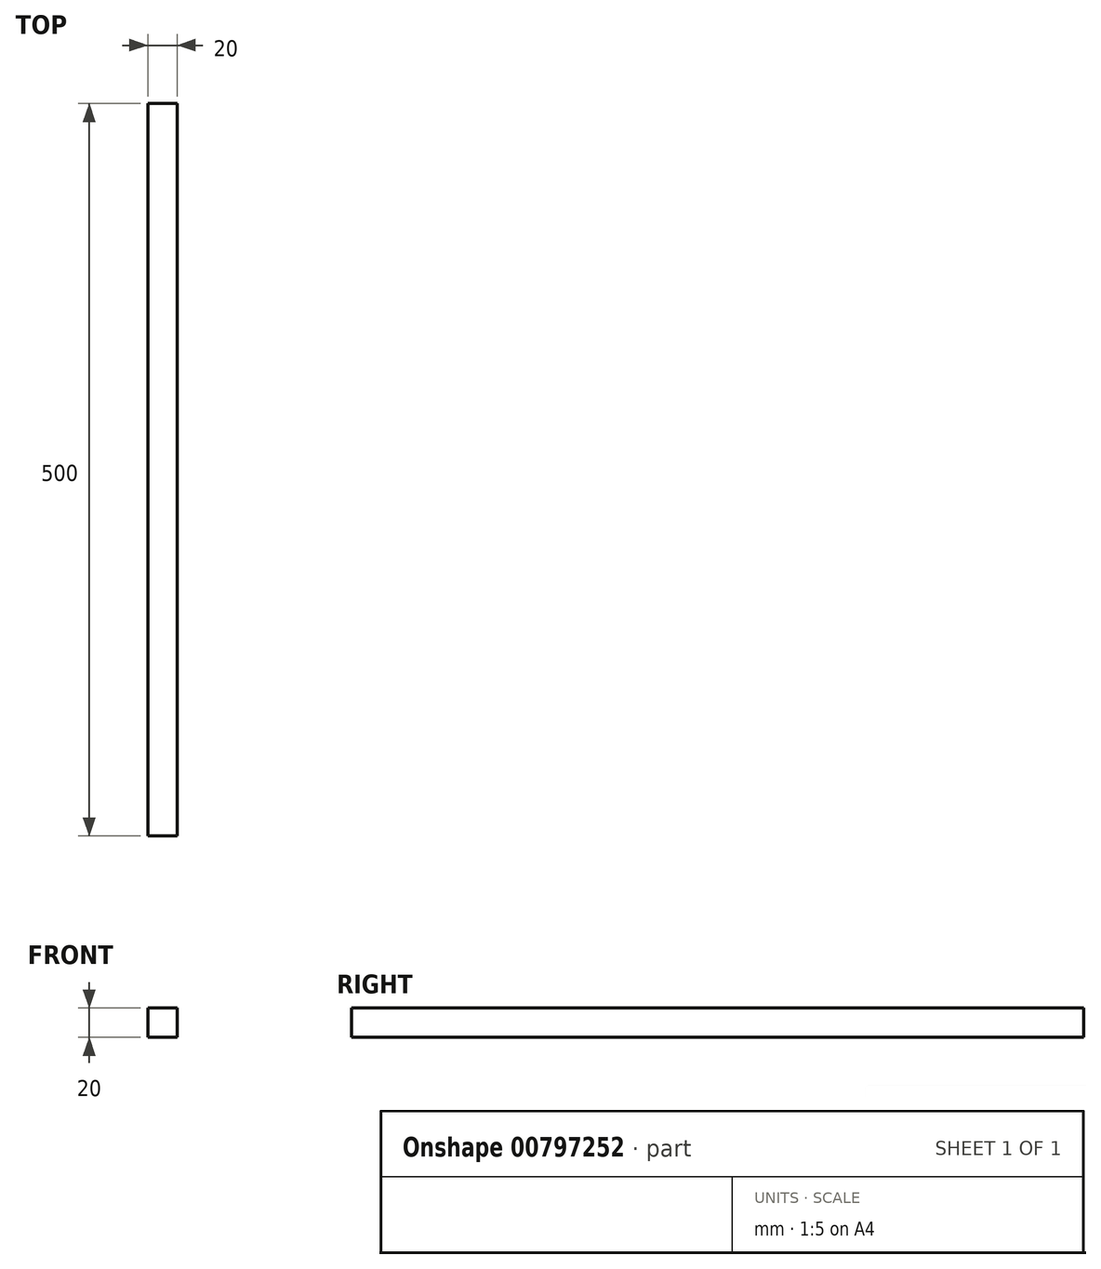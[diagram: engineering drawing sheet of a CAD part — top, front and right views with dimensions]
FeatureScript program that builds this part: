
annotation { "Feature Type Name" : "Feature", "Feature Type Description" : "" }
export const myFeature = defineFeature(function(context is Context, id is Id, definition is map)
    precondition{}
    {
        {
            var Q0;
            Q0=qCreatedBy(makeId("Front.planeOp"),FACE);
            var sketch = newSketch(context, id + "F0", { "sketchPlane" : qUnion([Q0])});
            skLineSegment(sketch, "E0.bottom", {"start": v(-68.37, 52.5) * mm, "end": v(-48.37, 52.5) * mm});
            skLineSegment(sketch, "E0.top", {"start": v(-68.37, 32.5) * mm, "end": v(-48.37, 32.5) * mm});
            skLineSegment(sketch, "E0.left", {"start": v(-68.37, 52.5) * mm, "end": v(-68.37, 32.5) * mm});
            skLineSegment(sketch, "E0.right", {"start": v(-48.37, 52.5) * mm, "end": v(-48.37, 32.5) * mm});
            skSolve(sketch);
        }
        {
            var Q0;
            Q0=qSketchRegion(id+"F0",true);
            extrude(context, id + "F1", {"entities" : qUnion([Q0]), "depth" : 500 * mm, "offsetDistance" : 25 * mm});
        }
        {
            var Q0;
            Q0=makeQuery(id+"F1.opExtrude","SWEPT_FACE",FACE,{"disambiguationData":[OSD([sQuery(id+"F0.wireOp",EDGE,"E0.bottom")])]});
            var sketch = newSketch(context, id + "F2", { "sketchPlane" : qUnion([Q0])});
            skLineSegment(sketch, "E1", {"start": v(-68.37, -100) * mm, "end": v(-48.37, -100) * mm, "construction": true});
            skLineSegment(sketch, "E2", {"start": v(-58.37, -100) * mm, "end": v(-58.37, 0) * mm, "construction": true});
            skCircle(sketch, "E3", {"center": v(-58.37, -100) * mm, "radius": 3.75 * mm, "construction": true});
            skSolve(sketch);
        }
    });
